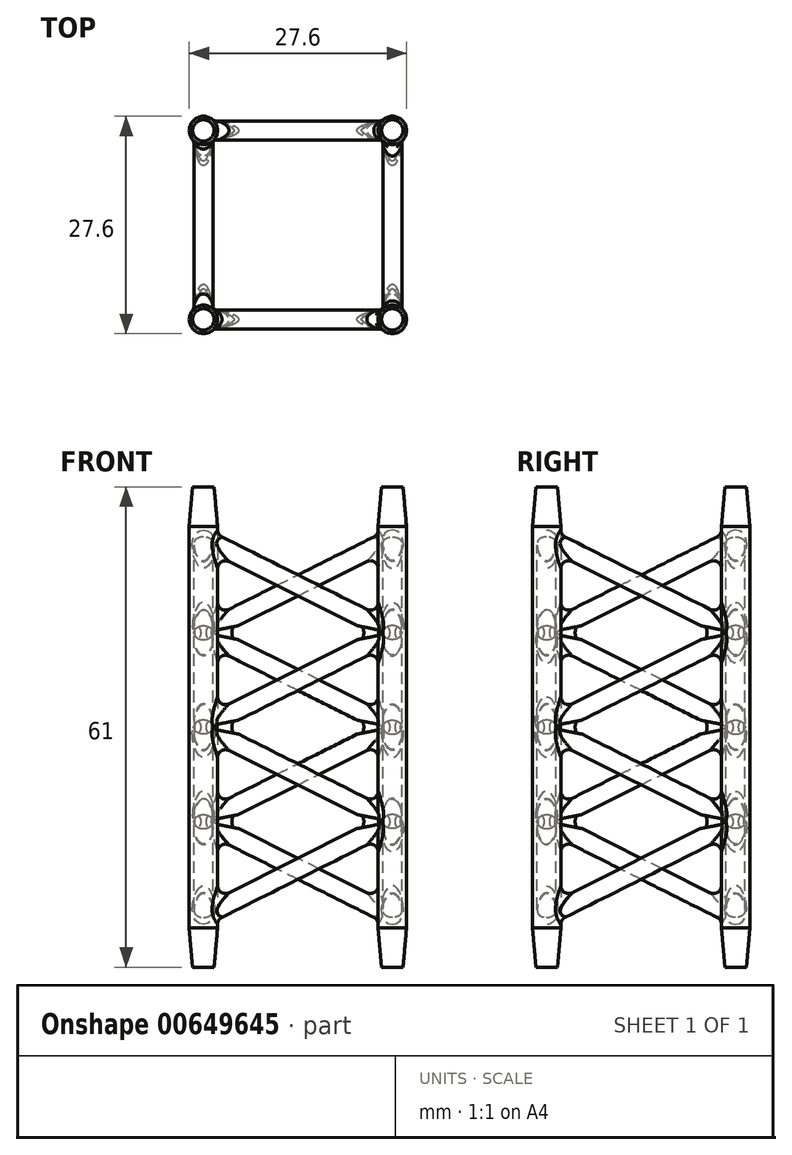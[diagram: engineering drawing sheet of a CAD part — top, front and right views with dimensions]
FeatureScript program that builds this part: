
annotation { "Feature Type Name" : "Feature", "Feature Type Description" : "" }
export const myFeature = defineFeature(function(context is Context, id is Id, definition is map)
    precondition{}
    {
        {
            var Q0;
            Q0=qCreatedBy(makeId("Top.planeOp"),FACE);
            var sketch = newSketch(context, id + "F0", { "sketchPlane" : qUnion([Q0])});
            skLineSegment(sketch, "E0", {"start": v(-12, -6.93) * mm, "end": v(12, -6.93) * mm});
            skLineSegment(sketch, "E1", {"start": v(12, -6.93) * mm, "end": v(0, 13.86) * mm});
            skLineSegment(sketch, "E2", {"start": v(0, 13.86) * mm, "end": v(-12, -6.93) * mm});
            skLineSegment(sketch, "E3", {"start": v(-6, 3.46) * mm, "end": v(12, -6.93) * mm});
            skLineSegment(sketch, "E4", {"start": v(6, 3.46) * mm, "end": v(-12, -6.93) * mm});
            skLineSegment(sketch, "E5", {"start": v(0, 13.86) * mm, "end": v(0, -6.93) * mm});
            skSolve(sketch);
        }
        {
            var Q0;
            Q0=qCreatedBy(makeId("Front.planeOp"),FACE);
            var sketch = newSketch(context, id + "F1", { "sketchPlane" : qUnion([Q0])});
            skLineSegment(sketch, "E6", {"start": v(0, 0) * mm, "end": v(0, 15.44) * mm});
            skSolve(sketch);
        }
        {
            var Q0;
            Q0=qCreatedBy(makeId("Top.planeOp"),FACE);
            var sketch = newSketch(context, id + "F2", { "sketchPlane" : qUnion([Q0])});
            skCircle(sketch, "E7", {"center": v(-12, -12) * mm, "radius": 1.8 * mm});
            skLineSegment(sketch, "E8.bottom", {"start": v(-12, 12) * mm, "end": v(12, 12) * mm, "construction": true});
            skLineSegment(sketch, "E8.top", {"start": v(-12, -12) * mm, "end": v(12, -12) * mm, "construction": true});
            skLineSegment(sketch, "E8.left", {"start": v(-12, 12) * mm, "end": v(-12, -12) * mm, "construction": true});
            skLineSegment(sketch, "E8.right", {"start": v(12, 12) * mm, "end": v(12, -12) * mm, "construction": true});
            skPoint(sketch, "E8.middle", {"position": v(0, 0) * mm});
            skSolve(sketch);
        }
        {
            var Q0;
            Q0=makeQuery(id+"F2.imprint","IMPRINT",FACE,{"disambiguationData":[TD([[makeQuery(id+"F2.imprint","IMPRINT",EDGE,{"derivedFrom":sQuery(id+"F2.wireOp",EDGE,"E7")}),1.0]])]});
            var Q1;
            Q1=sQuery(id+"F2.wireOp",EDGE,"E7");
            extrude(context, id + "F3", {"entities" : qUnion([Q0]), "surfaceEntities" : qUnion([Q1]), "depth" : 54.5 * mm, "offsetDistance" : 25 * mm, "hasSecondDirection" : true, "secondDirectionOppositeDirection" : true, "secondDirectionDepth" : 6.5 * mm});
        }
        {
            var Q0;
            Q0=sQuery(id+"F2.wireOp",EDGE,"E8.top");
            var Q1;
            Q1=sQuery(id+"F1.wireOp",EDGE,"E6");
            cPlane(context, id + "F4", {"entities" : qUnion([Q0, Q1]), "cplaneType" : CPlaneType.LINE_ANGLE, "offset" : 25 * mm, "angle" : 0 * degree, "width" : 150 * mm, "height" : 150 * mm});
        }
        {
            var Q0;
            Q0=qCreatedBy(id+"F4.planeOp",FACE);
            var sketch = newSketch(context, id + "F5", { "sketchPlane" : qUnion([Q0])});
            skLineSegment(sketch, "E9", {"start": v(-12, 0) * mm, "end": v(12, 12) * mm});
            skLineSegment(sketch, "E10", {"start": v(12, 12) * mm, "end": v(12, 0) * mm, "construction": true});
            skLineSegment(sketch, "E11", {"start": v(-12, 0) * mm, "end": v(-12, 24) * mm, "construction": true});
            skLineSegment(sketch, "E12", {"start": v(-12, 24) * mm, "end": v(12, 12) * mm});
            skLineSegment(sketch, "E13", {"start": v(-12, 24) * mm, "end": v(12, 36) * mm});
            skLineSegment(sketch, "E14", {"start": v(12, 36) * mm, "end": v(-12, 48) * mm});
            skLineSegment(sketch, "E15", {"start": v(-12, 48) * mm, "end": v(12, 60) * mm});
            skLineSegment(sketch, "E16", {"start": v(12, 60) * mm, "end": v(-12, 72) * mm});
            skLineSegment(sketch, "E17", {"start": v(-12, 72) * mm, "end": v(12, 84) * mm});
            skLineSegment(sketch, "E18", {"start": v(12, 84) * mm, "end": v(-12, 96) * mm});
            skLineSegment(sketch, "E19", {"start": v(-12, 96) * mm, "end": v(-12, 72) * mm, "construction": true});
            skLineSegment(sketch, "E20", {"start": v(-12, 48) * mm, "end": v(-12, 24) * mm, "construction": true});
            skLineSegment(sketch, "E21", {"start": v(-12, 48) * mm, "end": v(-12, 72) * mm, "construction": true});
            skLineSegment(sketch, "E22", {"start": v(12, 12) * mm, "end": v(12, 36) * mm, "construction": true});
            skLineSegment(sketch, "E23", {"start": v(12, 36) * mm, "end": v(12, 60) * mm, "construction": true});
            skLineSegment(sketch, "E24", {"start": v(12, 60) * mm, "end": v(12, 84) * mm, "construction": true});
            skLineSegment(sketch, "E25", {"start": v(-12, 96) * mm, "end": v(12, 108) * mm});
            skLineSegment(sketch, "E26", {"start": v(12, 108) * mm, "end": v(12, 84) * mm, "construction": true});
            skLineSegment(sketch, "E27", {"start": v(-12.25, 120) * mm, "end": v(12, 108) * mm});
            skLineSegment(sketch, "E28", {"start": v(-12.25, 120) * mm, "end": v(-12, 96) * mm, "construction": true});
            skLineSegment(sketch, "E29", {"start": v(12, 0) * mm, "end": v(-12, 0) * mm});
            skLineSegment(sketch, "E30", {"start": v(12, 108) * mm, "end": v(12, 132) * mm, "construction": true});
            skLineSegment(sketch, "E31", {"start": v(12, 132) * mm, "end": v(-12.25, 120) * mm});
            skLineSegment(sketch, "E32", {"start": v(-12.25, 120) * mm, "end": v(-12.25, 144) * mm, "construction": true});
            skLineSegment(sketch, "E33", {"start": v(12, 132) * mm, "end": v(-12.25, 144) * mm});
            skLineSegment(sketch, "E34", {"start": v(12, 144) * mm, "end": v(-12.25, 144) * mm});
            skLineSegment(sketch, "E35", {"start": v(12, 132) * mm, "end": v(12, 144) * mm, "construction": true});
            skSolve(sketch);
        }
        {
            var Q0;
            Q0=sQuery(id+"F5.wireOp",EDGE,"E9");
            var Q1;
            Q1=sQuery(id+"F5.wireOp",VERTEX,"E11.start");
            cPlane(context, id + "F6", {"entities" : qUnion([Q0, Q1]), "cplaneType" : CPlaneType.LINE_POINT, "offset" : 25 * mm, "width" : 150 * mm, "height" : 150 * mm});
        }
        {
            var Q0;
            Q0=qCreatedBy(id+"F6.planeOp",FACE);
            var sketch = newSketch(context, id + "F7", { "sketchPlane" : qUnion([Q0])});
            skCircle(sketch, "E36", {"center": v(-12, 5.37) * mm, "radius": 1.2 * mm});
            skSolve(sketch);
        }
        {
            var Q0;
            Q0=makeQuery(id+"F7.imprint","IMPRINT",FACE,{"disambiguationData":[TD([[makeQuery(id+"F7.imprint","IMPRINT",EDGE,{"derivedFrom":sQuery(id+"F7.wireOp",EDGE,"E36")}),1.0]])]});
            var Q1;
            Q1=sQuery(id+"F5.wireOp",EDGE,"E9");
            var Q2;
            Q2=sQuery(id+"F5.wireOp",EDGE,"E12");
            var Q3;
            Q3=sQuery(id+"F5.wireOp",EDGE,"E13");
            var Q4;
            Q4=sQuery(id+"F5.wireOp",EDGE,"E14");
            sweep(context, id + "F8", {"profiles" : qUnion([Q0]), "path" : qUnion([Q1, Q2, Q3, Q4])});
        }
        {
            var Q0;
            Q0=makeQuery(id+"F8.opSweep","SWEPT_FACE",FACE,{"disambiguationData":[OSD([sQuery(id+"F5.wireOp",EDGE,"E9"),sQuery(id+"F7.wireOp",EDGE,"E36")])]});
            var Q1;
            Q1=makeQuery(id+"F8.opSweep","SWEPT_FACE",FACE,{"disambiguationData":[OSD([sQuery(id+"F5.wireOp",EDGE,"E12"),sQuery(id+"F7.wireOp",EDGE,"E36")])]});
            var Q2;
            Q2=makeQuery(id+"F8.opSweep","SWEPT_FACE",FACE,{"disambiguationData":[OSD([sQuery(id+"F5.wireOp",EDGE,"E13"),sQuery(id+"F7.wireOp",EDGE,"E36")])]});
            var Q3;
            Q3=makeQuery(id+"F8.opSweep","SWEPT_FACE",FACE,{"disambiguationData":[OSD([sQuery(id+"F5.wireOp",EDGE,"E14"),sQuery(id+"F7.wireOp",EDGE,"E36")])]});
            var Q4;
            Q4=makeQuery(id+"F8.opSweep","SWEPT_FACE",FACE,{"disambiguationData":[OSD([sQuery(id+"F5.wireOp",EDGE,"E17"),sQuery(id+"F7.wireOp",EDGE,"E36")])]});
            var Q5;
            Q5=makeQuery(id+"F8.opSweep","SWEPT_FACE",FACE,{"disambiguationData":[OSD([sQuery(id+"F5.wireOp",EDGE,"E25"),sQuery(id+"F7.wireOp",EDGE,"E36")])]});
            var Q6;
            Q6=makeQuery(id+"F8.opSweep","SWEPT_FACE",FACE,{"disambiguationData":[OSD([sQuery(id+"F5.wireOp",EDGE,"E27"),sQuery(id+"F7.wireOp",EDGE,"E36")])]});
            var Q7;
            Q7=makeQuery(id+"F8.opSweep","SWEPT_FACE",FACE,{"disambiguationData":[OSD([sQuery(id+"F5.wireOp",EDGE,"E16"),sQuery(id+"F7.wireOp",EDGE,"E36")])]});
            var Q8;
            Q8=makeQuery(id+"F8.opSweep","SWEPT_FACE",FACE,{"disambiguationData":[OSD([sQuery(id+"F5.wireOp",EDGE,"E15"),sQuery(id+"F7.wireOp",EDGE,"E36")])]});
            var Q9;
            Q9=makeQuery(id+"F8.opSweep","SWEPT_FACE",FACE,{"disambiguationData":[OSD([sQuery(id+"F5.wireOp",EDGE,"E18"),sQuery(id+"F7.wireOp",EDGE,"E36")])]});
            var Q10;
            Q10=makeQuery(id+"F8.opSweep","MID_CAP_EDGE",EDGE,{"disambiguationData":[OSD([sQuery(id+"F5.wireOp",VERTEX,"E33.start"),sQuery(id+"F7.wireOp",EDGE,"E36")])],"capPos":12.0});
            var Q11;
            Q11=makeQuery(id+"F8.opSweep","MID_CAP_EDGE",EDGE,{"disambiguationData":[OSD([sQuery(id+"F5.wireOp",VERTEX,"E34.end"),sQuery(id+"F7.wireOp",EDGE,"E36")])],"capPos":13.0});
            fillet(context, id + "F9", {"entities" : qUnion([Q0, Q1, Q2, Q3, Q4, Q5, Q6, Q7, Q8, Q9, Q10, Q11]), "radius" : 1 * mm, "tangentPropagation" : true, "allowEdgeOverflow" : false});
        }
        {
            var Q0;
            Q0=makeQuery(id+"F3.opExtrude","SWEPT_BODY",BODY,{"disambiguationData":[OSD([sQuery(id+"F2.wireOp",EDGE,"E7")])]});
            var Q1;
            Q1=makeQuery(id+"F8.opSweep","SWEPT_BODY",BODY,{"disambiguationData":[OSD([sQuery(id+"F5.wireOp",EDGE,"E14"),sQuery(id+"F7.wireOp",EDGE,"E36")])]});
            booleanBodies(context, id + "F10", {"operationType" : BooleanOperationType.UNION, "tools" : qUnion([Q0, Q1])});
        }
        {
            var Q0;
            Q0=makeQuery(id+"F10.opBoolean","INTERSECT",EDGE,{"derivedFrom":[makeQuery(id+"F3.opExtrude","SWEPT_FACE",FACE,{"disambiguationData":[OSD([sQuery(id+"F2.wireOp",EDGE,"E7")])]}),makeQuery(id+"F8.opSweep","SWEPT_FACE",FACE,{"disambiguationData":[OSD([sQuery(id+"F5.wireOp",EDGE,"E14"),sQuery(id+"F7.wireOp",EDGE,"E36")])]})]});
            var Q1;
            Q1=makeQuery(id+"F10.opBoolean","INTERSECT",EDGE,{"derivedFrom":[makeQuery(id+"F3.opExtrude","SWEPT_FACE",FACE,{"disambiguationData":[OSD([sQuery(id+"F2.wireOp",EDGE,"E7")])]}),makeQuery(id+"F8.opSweep","SWEPT_FACE",FACE,{"disambiguationData":[OSD([sQuery(id+"F5.wireOp",EDGE,"E9"),sQuery(id+"F7.wireOp",EDGE,"E36")])]})]});
            var Q2;
            Q2=makeQuery(id+"F10.opBoolean","INTERSECT",EDGE,{"derivedFrom":[makeQuery(id+"F3.opExtrude","SWEPT_FACE",FACE,{"disambiguationData":[OSD([sQuery(id+"F2.wireOp",EDGE,"E7")])]}),makeQuery(id+"F8.opSweep","SWEPT_FACE",FACE,{"disambiguationData":[OSD([sQuery(id+"F5.wireOp",EDGE,"E12"),sQuery(id+"F7.wireOp",EDGE,"E36")])]})]});
            fillet(context, id + "F11", {"entities" : qUnion([Q0, Q1, Q2]), "radius" : 1 * mm, "tangentPropagation" : true, "allowEdgeOverflow" : false});
        }
        {
            var Q0;
            Q0=makeQuery(id+"FOFZZQhrRr9CB2q_1.opPattern","COPY",BODY,{"derivedFrom":makeQuery(id+"FBj1d7q4FQKIzEE_0.opExtrude","SWEPT_BODY",BODY,{"disambiguationData":[OSD([sQuery(id+"FcsWX7URlHym1KC_0.wireOp",EDGE,"24a714e4-7966-4e9e-99a7-43efdcecc9a9")])]}),"instanceName":"1"});
            var Q1;
            Q1=makeQuery(id+"FBj1d7q4FQKIzEE_0.opExtrude","SWEPT_BODY",BODY,{"disambiguationData":[OSD([sQuery(id+"FcsWX7URlHym1KC_0.wireOp",EDGE,"24a714e4-7966-4e9e-99a7-43efdcecc9a9")])]});
            var Q2;
            Q2=makeQuery(id+"F3.opExtrude","SWEPT_BODY",BODY,{"disambiguationData":[OSD([sQuery(id+"F2.wireOp",EDGE,"E7")])]});
            var Q3;
            Q3=makeQuery(id+"F8.opSweep","SWEPT_BODY",BODY,{"disambiguationData":[OSD([sQuery(id+"F5.wireOp",EDGE,"E27"),sQuery(id+"F7.wireOp",EDGE,"E36")])]});
            var Q4;
            Q4=sQuery(id+"F1.wireOp",EDGE,"E6");
            circularPattern(context, id + "F12", {"entities" : qUnion([Q0, Q1, Q2, Q3]), "axis" : qUnion([Q4]), "angle" : 360 * degree, "instanceCount" : 4, "equalSpace" : true});
        }
        {
            var Q0;
            Q0=makeQuery(id+"F3.opExtrude","SWEPT_BODY",BODY,{"disambiguationData":[OSD([sQuery(id+"F2.wireOp",EDGE,"E7")])]});
            var Q1;
            Q1=makeQuery(id+"F12.opPattern","COPY",BODY,{"derivedFrom":makeQuery(id+"F3.opExtrude","SWEPT_BODY",BODY,{"disambiguationData":[OSD([sQuery(id+"F2.wireOp",EDGE,"E7")])]}),"instanceName":"1"});
            var Q2;
            Q2=makeQuery(id+"F12.opPattern","COPY",BODY,{"derivedFrom":makeQuery(id+"F3.opExtrude","SWEPT_BODY",BODY,{"disambiguationData":[OSD([sQuery(id+"F2.wireOp",EDGE,"E7")])]}),"instanceName":"2"});
            var Q3;
            Q3=makeQuery(id+"F12.opPattern","COPY",BODY,{"derivedFrom":makeQuery(id+"F3.opExtrude","SWEPT_BODY",BODY,{"disambiguationData":[OSD([sQuery(id+"F2.wireOp",EDGE,"E7")])]}),"instanceName":"3"});
            booleanBodies(context, id + "F13", {"operationType" : BooleanOperationType.UNION, "tools" : qUnion([Q0, Q1, Q2, Q3])});
        }
        {
            var Q0;
            Q0=makeQuery(id+"F13.opBoolean","INTERSECT",EDGE,{"derivedFrom":[makeQuery(id+"F8.opSweep","SWEPT_FACE",FACE,{"disambiguationData":[OSD([sQuery(id+"F5.wireOp",EDGE,"E12"),sQuery(id+"F7.wireOp",EDGE,"E36")])]}),makeQuery(id+"F12.opPattern","COPY",FACE,{"derivedFrom":makeQuery(id+"F3.opExtrude","SWEPT_FACE",FACE,{"disambiguationData":[OSD([sQuery(id+"F2.wireOp",EDGE,"E7")])]}),"instanceName":"1"})]});
            var Q1;
            Q1=makeQuery(id+"F13.opBoolean","INTERSECT",EDGE,{"derivedFrom":[makeQuery(id+"F8.opSweep","SWEPT_FACE",FACE,{"disambiguationData":[OSD([sQuery(id+"F5.wireOp",EDGE,"E13"),sQuery(id+"F7.wireOp",EDGE,"E36")])]}),makeQuery(id+"F12.opPattern","COPY",FACE,{"derivedFrom":makeQuery(id+"F3.opExtrude","SWEPT_FACE",FACE,{"disambiguationData":[OSD([sQuery(id+"F2.wireOp",EDGE,"E7")])]}),"instanceName":"1"})]});
            var Q2;
            Q2=makeQuery(id+"F13.opBoolean","INTERSECT",EDGE,{"derivedFrom":[makeQuery(id+"F12.opPattern","COPY",FACE,{"derivedFrom":makeQuery(id+"F8.opSweep","SWEPT_FACE",FACE,{"disambiguationData":[OSD([sQuery(id+"F5.wireOp",EDGE,"E9"),sQuery(id+"F7.wireOp",EDGE,"E36")])]}),"instanceName":"1"}),makeQuery(id+"F12.opPattern","COPY",FACE,{"derivedFrom":makeQuery(id+"F3.opExtrude","SWEPT_FACE",FACE,{"disambiguationData":[OSD([sQuery(id+"F2.wireOp",EDGE,"E7")])]}),"instanceName":"2"})]});
            var Q3;
            Q3=makeQuery(id+"F13.opBoolean","INTERSECT",EDGE,{"derivedFrom":[makeQuery(id+"F12.opPattern","COPY",FACE,{"derivedFrom":makeQuery(id+"F8.opSweep","SWEPT_FACE",FACE,{"disambiguationData":[OSD([sQuery(id+"F5.wireOp",EDGE,"E14"),sQuery(id+"F7.wireOp",EDGE,"E36")])]}),"instanceName":"1"}),makeQuery(id+"F12.opPattern","COPY",FACE,{"derivedFrom":makeQuery(id+"F3.opExtrude","SWEPT_FACE",FACE,{"disambiguationData":[OSD([sQuery(id+"F2.wireOp",EDGE,"E7")])]}),"instanceName":"2"})]});
            var Q4;
            Q4=makeQuery(id+"F13.opBoolean","INTERSECT",EDGE,{"derivedFrom":[makeQuery(id+"F12.opPattern","COPY",FACE,{"derivedFrom":makeQuery(id+"F8.opSweep","SWEPT_FACE",FACE,{"disambiguationData":[OSD([sQuery(id+"F5.wireOp",EDGE,"E14"),sQuery(id+"F7.wireOp",EDGE,"E36")])]}),"instanceName":"2"}),makeQuery(id+"F12.opPattern","COPY",FACE,{"derivedFrom":makeQuery(id+"F3.opExtrude","SWEPT_FACE",FACE,{"disambiguationData":[OSD([sQuery(id+"F2.wireOp",EDGE,"E7")])]}),"instanceName":"3"})]});
            var Q5;
            Q5=makeQuery(id+"F13.opBoolean","INTERSECT",EDGE,{"derivedFrom":[makeQuery(id+"F12.opPattern","COPY",FACE,{"derivedFrom":makeQuery(id+"F8.opSweep","SWEPT_FACE",FACE,{"disambiguationData":[OSD([sQuery(id+"F5.wireOp",EDGE,"E12"),sQuery(id+"F7.wireOp",EDGE,"E36")])]}),"instanceName":"2"}),makeQuery(id+"F12.opPattern","COPY",FACE,{"derivedFrom":makeQuery(id+"F3.opExtrude","SWEPT_FACE",FACE,{"disambiguationData":[OSD([sQuery(id+"F2.wireOp",EDGE,"E7")])]}),"instanceName":"3"})]});
            var Q6;
            Q6=makeQuery(id+"F13.opBoolean","INTERSECT",EDGE,{"derivedFrom":[makeQuery(id+"F3.opExtrude","SWEPT_FACE",FACE,{"disambiguationData":[OSD([sQuery(id+"F2.wireOp",EDGE,"E7")])]}),makeQuery(id+"F12.opPattern","COPY",FACE,{"derivedFrom":makeQuery(id+"F8.opSweep","SWEPT_FACE",FACE,{"disambiguationData":[OSD([sQuery(id+"F5.wireOp",EDGE,"E14"),sQuery(id+"F7.wireOp",EDGE,"E36")])]}),"instanceName":"3"})]});
            var Q7;
            Q7=makeQuery(id+"F13.opBoolean","INTERSECT",EDGE,{"derivedFrom":[makeQuery(id+"F3.opExtrude","SWEPT_FACE",FACE,{"disambiguationData":[OSD([sQuery(id+"F2.wireOp",EDGE,"E7")])]}),makeQuery(id+"F12.opPattern","COPY",FACE,{"derivedFrom":makeQuery(id+"F8.opSweep","SWEPT_FACE",FACE,{"disambiguationData":[OSD([sQuery(id+"F5.wireOp",EDGE,"E12"),sQuery(id+"F7.wireOp",EDGE,"E36")])]}),"instanceName":"3"})]});
            fillet(context, id + "F14", {"entities" : qUnion([Q0, Q1, Q2, Q3, Q4, Q5, Q6, Q7]), "radius" : 1 * mm, "tangentPropagation" : true, "allowEdgeOverflow" : false});
        }
        {
            var Q0;
            Q0=makeQuery(id+"F3.opExtrude","CAP_EDGE",EDGE,{"disambiguationData":[OSD([sQuery(id+"F2.wireOp",EDGE,"E7")])],"isStart":true});
            var Q1;
            Q1=makeQuery(id+"F12.opPattern","COPY",EDGE,{"derivedFrom":makeQuery(id+"F3.opExtrude","CAP_EDGE",EDGE,{"disambiguationData":[OSD([sQuery(id+"F2.wireOp",EDGE,"E7")])],"isStart":true}),"instanceName":"1"});
            var Q2;
            Q2=makeQuery(id+"F12.opPattern","COPY",EDGE,{"derivedFrom":makeQuery(id+"F3.opExtrude","CAP_EDGE",EDGE,{"disambiguationData":[OSD([sQuery(id+"F2.wireOp",EDGE,"E7")])],"isStart":true}),"instanceName":"2"});
            var Q3;
            Q3=makeQuery(id+"F12.opPattern","COPY",EDGE,{"derivedFrom":makeQuery(id+"F3.opExtrude","CAP_EDGE",EDGE,{"disambiguationData":[OSD([sQuery(id+"F2.wireOp",EDGE,"E7")])],"isStart":true}),"instanceName":"3"});
            chamfer(context, id + "F15", {"entities" : qUnion([Q0, Q1, Q2, Q3]), "chamferType" : ChamferType.OFFSET_ANGLE, "width" : 5 * mm, "oppositeDirection" : false, "angle" : 5 * degree, "tangentPropagation" : true});
        }
        {
            var Q0;
            Q0=makeQuery(id+"F12.opPattern","COPY",EDGE,{"derivedFrom":makeQuery(id+"F3.opExtrude","CAP_EDGE",EDGE,{"disambiguationData":[OSD([sQuery(id+"F2.wireOp",EDGE,"E7")])],"isStart":false}),"instanceName":"1"});
            var Q1;
            Q1=makeQuery(id+"F12.opPattern","COPY",EDGE,{"derivedFrom":makeQuery(id+"F3.opExtrude","CAP_EDGE",EDGE,{"disambiguationData":[OSD([sQuery(id+"F2.wireOp",EDGE,"E7")])],"isStart":false}),"instanceName":"2"});
            var Q2;
            Q2=makeQuery(id+"F3.opExtrude","CAP_EDGE",EDGE,{"disambiguationData":[OSD([sQuery(id+"F2.wireOp",EDGE,"E7")])],"isStart":false});
            var Q3;
            Q3=makeQuery(id+"F12.opPattern","COPY",EDGE,{"derivedFrom":makeQuery(id+"F3.opExtrude","CAP_EDGE",EDGE,{"disambiguationData":[OSD([sQuery(id+"F2.wireOp",EDGE,"E7")])],"isStart":false}),"instanceName":"3"});
            chamfer(context, id + "F16", {"entities" : qUnion([Q0, Q1, Q2, Q3]), "chamferType" : ChamferType.OFFSET_ANGLE, "width" : 5 * mm, "oppositeDirection" : true, "angle" : 5 * degree, "tangentPropagation" : true});
        }
    });
